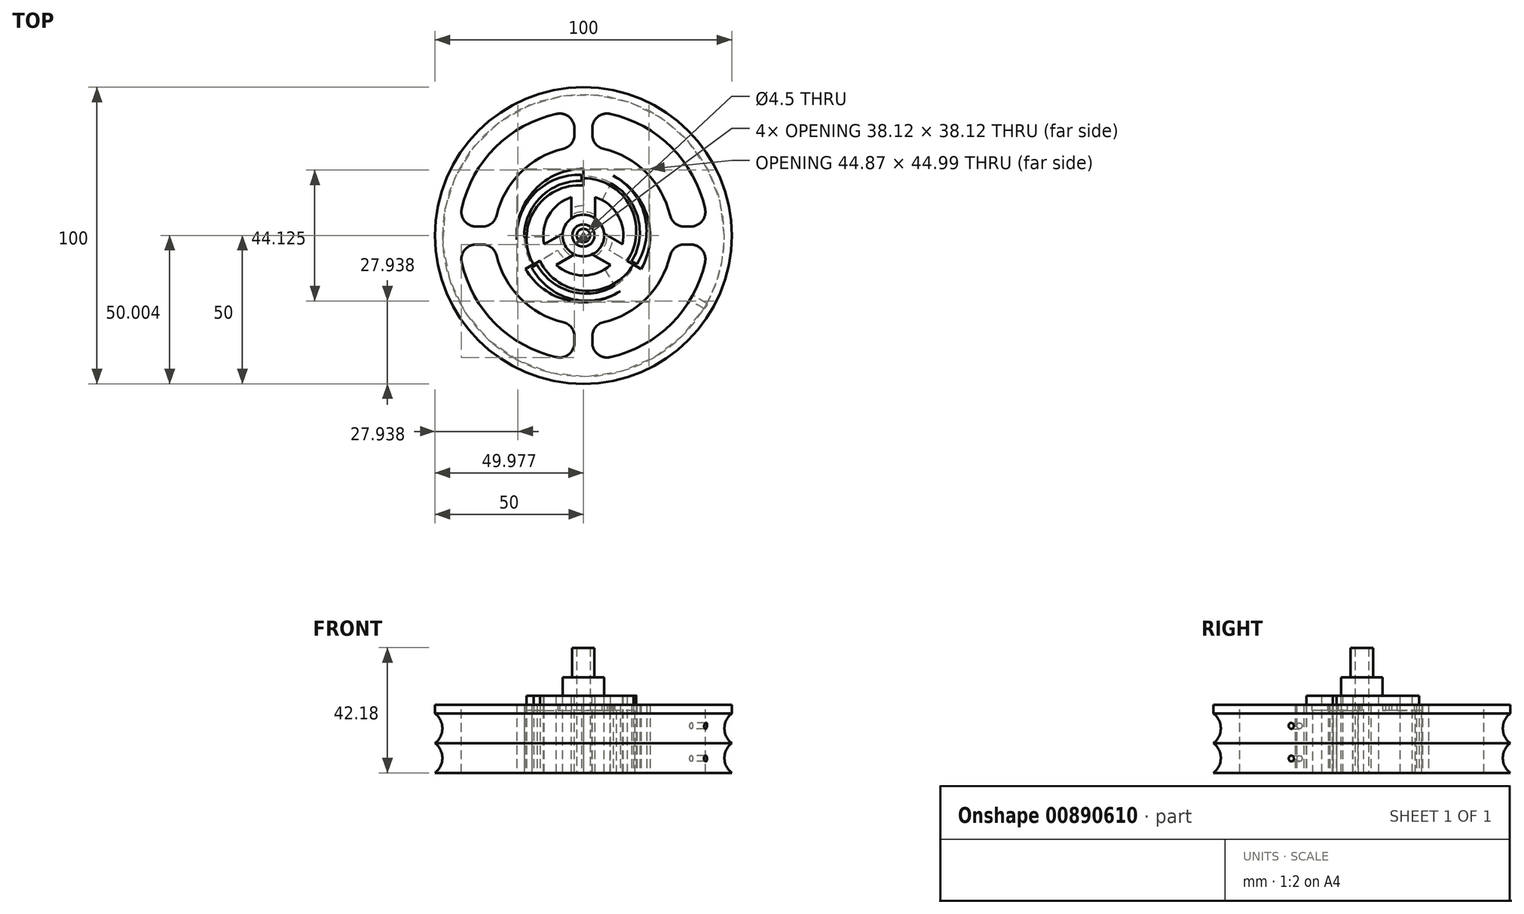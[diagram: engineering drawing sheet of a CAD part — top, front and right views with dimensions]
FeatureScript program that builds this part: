
annotation { "Feature Type Name" : "Feature", "Feature Type Description" : "" }
export const myFeature = defineFeature(function(context is Context, id is Id, definition is map)
    precondition{}
    {
        {
            var Q0;
            Q0=qCreatedBy(makeId("Top.planeOp"),FACE);
            var sketch = newSketch(context, id + "F0", { "sketchPlane" : qUnion([Q0])});
            skCircle(sketch, "E0", {"center": v(0, 0) * mm, "radius": 50 * mm});
            skLineSegment(sketch, "E1", {"start": v(0.67, 20.46) * mm, "end": v(0.67, 18.46) * mm});
            skArc(sketch, "E2", {"start": v(22.46, -1.4) * mm, "mid": v(16.36, 14.31) * mm, "end": v(0.67, 20.46) * mm});
            skArc(sketch, "E3", {"start": v(19.96, -1.24) * mm, "mid": v(14.55, 12.75) * mm, "end": v(0.67, 18.46) * mm});
            skArc(sketch, "E4", {"start": v(22.46, -1.4) * mm, "mid": v(16.4, 15.4) * mm, "end": v(0, 22.5) * mm});
            skArc(sketch, "E5", {"start": v(17.32, -10) * mm, "mid": v(19.15, -5.77) * mm, "end": v(19.96, -1.24) * mm});
            skLineSegment(sketch, "E6", {"start": v(0, 22.5) * mm, "end": v(0, 20) * mm});
            skArc(sketch, "E7.1.0", {"start": v(-10.02, 20.15) * mm, "mid": v(-21.54, 6.5) * mm, "end": v(-19.49, -11.25) * mm});
            skArc(sketch, "E7.1.1", {"start": v(0, 20) * mm, "mid": v(-4.58, 19.47) * mm, "end": v(-8.9, 17.9) * mm});
            skArc(sketch, "E7.1.2", {"start": v(-10.02, 20.15) * mm, "mid": v(-20.57, 7.01) * mm, "end": v(-18.05, -9.65) * mm});
            skArc(sketch, "E7.1.3", {"start": v(-8.9, 17.9) * mm, "mid": v(-18.32, 6.22) * mm, "end": v(-16.32, -8.65) * mm});
            skLineSegment(sketch, "E7.1.4", {"start": v(-18.05, -9.65) * mm, "end": v(-16.32, -8.65) * mm});
            skLineSegment(sketch, "E7.1.5", {"start": v(-19.49, -11.25) * mm, "end": v(-17.32, -10) * mm});
            skArc(sketch, "E7.2.0", {"start": v(-12.44, -18.75) * mm, "mid": v(5.15, -21.9) * mm, "end": v(19.49, -11.25) * mm});
            skArc(sketch, "E7.2.1", {"start": v(-17.32, -10) * mm, "mid": v(-14.57, -13.7) * mm, "end": v(-11.05, -16.67) * mm});
            skArc(sketch, "E7.2.2", {"start": v(-12.44, -18.75) * mm, "mid": v(4.21, -21.32) * mm, "end": v(17.38, -10.81) * mm});
            skArc(sketch, "E7.2.3", {"start": v(-11.05, -16.67) * mm, "mid": v(3.77, -18.98) * mm, "end": v(15.65, -9.81) * mm});
            skLineSegment(sketch, "E7.2.4", {"start": v(17.38, -10.81) * mm, "end": v(15.65, -9.81) * mm});
            skLineSegment(sketch, "E7.2.5", {"start": v(19.49, -11.25) * mm, "end": v(17.32, -10) * mm});
            skLineSegment(sketch, "E8", {"start": v(0, 19.35) * mm, "end": v(0, 16.88) * mm});
            skLineSegment(sketch, "E9", {"start": v(-17.32, -10) * mm, "end": v(0, 0) * mm, "construction": true});
            skArc(sketch, "E10", {"start": v(0, 19.35) * mm, "mid": v(-15.76, 9.87) * mm, "end": v(-14.71, -8.5) * mm});
            skArc(sketch, "E11.1.0", {"start": v(-16.85, -9.73) * mm, "mid": v(-0.76, -18.64) * mm, "end": v(14.62, -8.55) * mm});
            skLineSegment(sketch, "E11.1.1", {"start": v(-16.85, -9.73) * mm, "end": v(-14.71, -8.5) * mm});
            skArc(sketch, "E11.2.0", {"start": v(16.76, -9.78) * mm, "mid": v(16.43, 8.6) * mm, "end": v(0, 16.88) * mm});
            skLineSegment(sketch, "E11.2.1", {"start": v(16.76, -9.78) * mm, "end": v(14.62, -8.55) * mm});
            skPoint(sketch, "E11.center", {"position": v(-0.03, -0.05) * mm});
            skLineSegment(sketch, "E12", {"start": v(-16.85, -9.73) * mm, "end": v(-17.19, -9.15) * mm, "construction": true});
            skLineSegment(sketch, "E13", {"start": v(0, 0) * mm, "end": v(22.46, -1.4) * mm, "construction": true});
            skLineSegment(sketch, "E14.1.0", {"start": v(0, 0) * mm, "end": v(-10.02, 20.15) * mm, "construction": true});
            skLineSegment(sketch, "E14.2.0", {"start": v(0, 0) * mm, "end": v(-12.44, -18.75) * mm, "construction": true});
            skLineSegment(sketch, "E15.1.0", {"start": v(17.32, -10) * mm, "end": v(0, 0) * mm, "construction": true});
            skLineSegment(sketch, "E15.2.0", {"start": v(0, 20) * mm, "end": v(0, 0) * mm, "construction": true});
            skSolve(sketch);
        }
        {
            var Q0;
            Q0=makeQuery(id+"F0.imprint","IMPRINT",FACE,{"disambiguationData":[TD([[makeQuery(id+"F0.imprint","IMPRINT",EDGE,{"derivedFrom":sQuery(id+"F0.wireOp",EDGE,"E0")}),1.0]])]});
            extrude(context, id + "F1", {"entities" : qUnion([Q0]), "depth" : 21 * mm, "offsetDistance" : 25 * mm});
        }
        {
            var Q0;
            {var subQ3=sQuery(id+"F0.wireOp",EDGE,"E10");var subQ7=sQuery(id+"F0.wireOp",EDGE,"E8");var subQ8=makeQuery(id+"F0.imprint","INTERSECT",VERTEX,{"derivedFrom":[subQ7,subQ3]});Q0=makeQuery(id+"F0.imprint","IMPRINT",FACE,{"disambiguationData":[TD([[makeQuery(id+"F0.imprint","IMPRINT",EDGE,{"disambiguationData":[TD([[subQ8,-1.0]])],"derivedFrom":subQ7}),-1.0]])]});}
            extrude(context, id + "F2", {"entities" : qUnion([Q0]), "depth" : 26 * mm, "offsetDistance" : 25 * mm});
        }
        {
            var Q0;
            Q0=qCreatedBy(makeId("Right.planeOp"),FACE);
            var sketch = newSketch(context, id + "F3", { "sketchPlane" : qUnion([Q0])});
            skLineSegment(sketch, "E16", {"start": v(0, 0) * mm, "end": v(50, 0) * mm});
            skLineSegment(sketch, "E17", {"start": v(50, 0) * mm, "end": v(50, 20) * mm});
            skLineSegment(sketch, "E18", {"start": v(50, 20) * mm, "end": v(0, 20) * mm});
            skLineSegment(sketch, "E19", {"start": v(0, 20) * mm, "end": v(0, 0) * mm});
            skArc(sketch, "E20", {"start": v(50, 20) * mm, "mid": v(47.53, 15) * mm, "end": v(50, 10) * mm});
            skArc(sketch, "E21", {"start": v(50, 10) * mm, "mid": v(47.53, 5) * mm, "end": v(50, 0) * mm});
            skSolve(sketch);
        }
        {
            var Q0;
            {var subQ0=sQuery(id+"F3.wireOp",EDGE,"E20");Q0=makeQuery(id+"F3.imprint","IMPRINT",FACE,{"disambiguationData":[TD([[makeQuery(id+"F3.imprint","IMPRINT",EDGE,{"derivedFrom":subQ0}),1.0]])]});}
            var Q1;
            {var subQ0=sQuery(id+"F3.wireOp",EDGE,"E21");Q1=makeQuery(id+"F3.imprint","IMPRINT",FACE,{"disambiguationData":[TD([[makeQuery(id+"F3.imprint","IMPRINT",EDGE,{"derivedFrom":subQ0}),1.0]])]});}
            var Q2;
            Q2=sQuery(id+"F3.wireOp",EDGE,"E19");
            revolve(context, id + "F4", {"operationType" : NewBodyOperationType.REMOVE, "surfaceOperationType" : NewSurfaceOperationType.NEW, "entities" : qUnion([Q0, Q1]), "axis" : qUnion([Q2]), "revolveType" : RevolveType.FULL, "oppositeDirection" : true});
        }
        {
            var Q0;
            Q0=makeQuery(id+"F2.opExtrude","CAP_FACE",FACE,{"disambiguationData":[OSD([sQuery(id+"F0.wireOp",EDGE,"E8"),sQuery(id+"F0.wireOp",EDGE,"E10"),sQuery(id+"F0.wireOp",EDGE,"E11.1.0"),sQuery(id+"F0.wireOp",EDGE,"E11.1.1"),sQuery(id+"F0.wireOp",EDGE,"E11.2.0"),sQuery(id+"F0.wireOp",EDGE,"E11.2.1")])],"isStart":true});
            var sketch = newSketch(context, id + "F5", { "sketchPlane" : qUnion([Q0])});
            skCircle(sketch, "E22", {"center": v(0, 0) * mm, "radius": 2.25 * mm});
            skSolve(sketch);
        }
        {
            var Q0;
            Q0=makeQuery(id+"F5.imprint","IMPRINT",FACE,{"disambiguationData":[TD([[makeQuery(id+"F5.imprint","IMPRINT",EDGE,{"derivedFrom":sQuery(id+"F5.wireOp",EDGE,"E22")}),1.0]])]});
            extrude(context, id + "F6", {"entities" : qUnion([Q0]), "operationType" : NewBodyOperationType.REMOVE, "oppositeDirection" : true, "depth" : 100 * mm, "offsetDistance" : 25 * mm});
        }
        {
            var Q0;
            Q0=qCreatedBy(makeId("Right.planeOp"),FACE);
            cPlane(context, id + "F7", {"entities" : qUnion([Q0]), "cplaneType" : CPlaneType.OFFSET, "offset" : 50 * mm, "width" : 150 * mm, "height" : 150 * mm});
        }
        {
            var Q0;
            Q0=makeQuery(id+"F2.opExtrude","SWEPT_BODY",BODY,{"disambiguationData":[OSD([sQuery(id+"F0.wireOp",EDGE,"E8"),sQuery(id+"F0.wireOp",EDGE,"E10"),sQuery(id+"F0.wireOp",EDGE,"E11.1.0"),sQuery(id+"F0.wireOp",EDGE,"E11.1.1"),sQuery(id+"F0.wireOp",EDGE,"E11.2.0"),sQuery(id+"F0.wireOp",EDGE,"E11.2.1")])]});
            var Q1;
            Q1=makeQuery(id+"F1.opExtrude","SWEPT_BODY",BODY,{"disambiguationData":[OSD([sQuery(id+"F0.wireOp",EDGE,"E0"),sQuery(id+"F0.wireOp",EDGE,"E1"),sQuery(id+"F0.wireOp",EDGE,"E2"),sQuery(id+"F0.wireOp",EDGE,"E3"),sQuery(id+"F0.wireOp",EDGE,"E4"),sQuery(id+"F0.wireOp",EDGE,"E5"),sQuery(id+"F0.wireOp",EDGE,"E6"),sQuery(id+"F0.wireOp",EDGE,"E7.1.0"),sQuery(id+"F0.wireOp",EDGE,"E7.1.1"),sQuery(id+"F0.wireOp",EDGE,"E7.1.2"),sQuery(id+"F0.wireOp",EDGE,"E7.1.3"),sQuery(id+"F0.wireOp",EDGE,"E7.1.4"),sQuery(id+"F0.wireOp",EDGE,"E7.1.5"),sQuery(id+"F0.wireOp",EDGE,"E7.2.0"),sQuery(id+"F0.wireOp",EDGE,"E7.2.1"),sQuery(id+"F0.wireOp",EDGE,"E7.2.2"),sQuery(id+"F0.wireOp",EDGE,"E7.2.3"),sQuery(id+"F0.wireOp",EDGE,"E7.2.4"),sQuery(id+"F0.wireOp",EDGE,"E7.2.5")])]});
            var Q2;
            Q2=qCreatedBy(id+"F7.planeOp",FACE);
            mirror(context, id + "F8", {"entities" : qUnion([Q0, Q1]), "mirrorPlane" : qUnion([Q2])});
        }
        {
            var Q0;
            Q0=makeQuery(id+"F8.opPattern","COPY",BODY,{"derivedFrom":makeQuery(id+"F2.opExtrude","SWEPT_BODY",BODY,{"disambiguationData":[OSD([sQuery(id+"F0.wireOp",EDGE,"E8"),sQuery(id+"F0.wireOp",EDGE,"E10"),sQuery(id+"F0.wireOp",EDGE,"E11.1.0"),sQuery(id+"F0.wireOp",EDGE,"E11.1.1"),sQuery(id+"F0.wireOp",EDGE,"E11.2.0"),sQuery(id+"F0.wireOp",EDGE,"E11.2.1")])]}),"instanceName":"1"});
            var Q1;
            Q1=makeQuery(id+"F8.opPattern","COPY",BODY,{"derivedFrom":makeQuery(id+"F1.opExtrude","SWEPT_BODY",BODY,{"disambiguationData":[OSD([sQuery(id+"F0.wireOp",EDGE,"E0"),sQuery(id+"F0.wireOp",EDGE,"E1"),sQuery(id+"F0.wireOp",EDGE,"E2"),sQuery(id+"F0.wireOp",EDGE,"E3"),sQuery(id+"F0.wireOp",EDGE,"E4"),sQuery(id+"F0.wireOp",EDGE,"E5"),sQuery(id+"F0.wireOp",EDGE,"E6"),sQuery(id+"F0.wireOp",EDGE,"E7.1.0"),sQuery(id+"F0.wireOp",EDGE,"E7.1.1"),sQuery(id+"F0.wireOp",EDGE,"E7.1.2"),sQuery(id+"F0.wireOp",EDGE,"E7.1.3"),sQuery(id+"F0.wireOp",EDGE,"E7.1.4"),sQuery(id+"F0.wireOp",EDGE,"E7.1.5"),sQuery(id+"F0.wireOp",EDGE,"E7.2.0"),sQuery(id+"F0.wireOp",EDGE,"E7.2.1"),sQuery(id+"F0.wireOp",EDGE,"E7.2.2"),sQuery(id+"F0.wireOp",EDGE,"E7.2.3"),sQuery(id+"F0.wireOp",EDGE,"E7.2.4"),sQuery(id+"F0.wireOp",EDGE,"E7.2.5")])]}),"instanceName":"1"});
            var Q2;
            Q2=qCreatedBy(id+"F7.planeOp",FACE);
            mirror(context, id + "F9", {"operationType" : NewBodyOperationType.REMOVE, "entities" : qUnion([Q0, Q1]), "mirrorPlane" : qUnion([Q2])});
        }
        {
            var Q0;
            Q0=makeQuery(id+"F8.opPattern","COPY",BODY,{"derivedFrom":makeQuery(id+"F2.opExtrude","SWEPT_BODY",BODY,{"disambiguationData":[OSD([sQuery(id+"F0.wireOp",EDGE,"E8"),sQuery(id+"F0.wireOp",EDGE,"E10"),sQuery(id+"F0.wireOp",EDGE,"E11.1.0"),sQuery(id+"F0.wireOp",EDGE,"E11.1.1"),sQuery(id+"F0.wireOp",EDGE,"E11.2.0"),sQuery(id+"F0.wireOp",EDGE,"E11.2.1")])]}),"instanceName":"1"});
            var Q1;
            Q1=makeQuery(id+"F8.opPattern","COPY",BODY,{"derivedFrom":makeQuery(id+"F1.opExtrude","SWEPT_BODY",BODY,{"disambiguationData":[OSD([sQuery(id+"F0.wireOp",EDGE,"E0"),sQuery(id+"F0.wireOp",EDGE,"E1"),sQuery(id+"F0.wireOp",EDGE,"E2"),sQuery(id+"F0.wireOp",EDGE,"E3"),sQuery(id+"F0.wireOp",EDGE,"E4"),sQuery(id+"F0.wireOp",EDGE,"E5"),sQuery(id+"F0.wireOp",EDGE,"E6"),sQuery(id+"F0.wireOp",EDGE,"E7.1.0"),sQuery(id+"F0.wireOp",EDGE,"E7.1.1"),sQuery(id+"F0.wireOp",EDGE,"E7.1.2"),sQuery(id+"F0.wireOp",EDGE,"E7.1.3"),sQuery(id+"F0.wireOp",EDGE,"E7.1.4"),sQuery(id+"F0.wireOp",EDGE,"E7.1.5"),sQuery(id+"F0.wireOp",EDGE,"E7.2.0"),sQuery(id+"F0.wireOp",EDGE,"E7.2.1"),sQuery(id+"F0.wireOp",EDGE,"E7.2.2"),sQuery(id+"F0.wireOp",EDGE,"E7.2.3"),sQuery(id+"F0.wireOp",EDGE,"E7.2.4"),sQuery(id+"F0.wireOp",EDGE,"E7.2.5")])]}),"instanceName":"1"});
            transform(context, id + "F10", {"entities" : qUnion([Q0, Q1]), "transformType" : TransformType.TRANSLATION_3D, "dx" : -100 * mm, "dy" : 0 * mm, "dz" : 0 * mm, "makeCopy" : false});
        }
        {
            var Q0;
            Q0=makeQuery(id+"F8.opPattern","COPY",FACE,{"derivedFrom":makeQuery(id+"F1.opExtrude","CAP_FACE",FACE,{"disambiguationData":[OSD([sQuery(id+"F0.wireOp",EDGE,"E0"),sQuery(id+"F0.wireOp",EDGE,"E1"),sQuery(id+"F0.wireOp",EDGE,"E2"),sQuery(id+"F0.wireOp",EDGE,"E3"),sQuery(id+"F0.wireOp",EDGE,"E4"),sQuery(id+"F0.wireOp",EDGE,"E5"),sQuery(id+"F0.wireOp",EDGE,"E6"),sQuery(id+"F0.wireOp",EDGE,"E7.1.0"),sQuery(id+"F0.wireOp",EDGE,"E7.1.1"),sQuery(id+"F0.wireOp",EDGE,"E7.1.2"),sQuery(id+"F0.wireOp",EDGE,"E7.1.3"),sQuery(id+"F0.wireOp",EDGE,"E7.1.4"),sQuery(id+"F0.wireOp",EDGE,"E7.1.5"),sQuery(id+"F0.wireOp",EDGE,"E7.2.0"),sQuery(id+"F0.wireOp",EDGE,"E7.2.1"),sQuery(id+"F0.wireOp",EDGE,"E7.2.2"),sQuery(id+"F0.wireOp",EDGE,"E7.2.3"),sQuery(id+"F0.wireOp",EDGE,"E7.2.4"),sQuery(id+"F0.wireOp",EDGE,"E7.2.5")])],"isStart":false}),"instanceName":"1"});
            var sketch = newSketch(context, id + "F11", { "sketchPlane" : qUnion([Q0])});
            skCircle(sketch, "E23", {"center": v(0, 0) * mm, "radius": 8 * mm});
            skCircle(sketch, "E24", {"center": v(0, 0) * mm, "radius": 10 * mm});
            skLineSegment(sketch, "E25", {"start": v(0, 20) * mm, "end": v(0, 10) * mm});
            skLineSegment(sketch, "E26", {"start": v(0, 10) * mm, "end": v(0, 0) * mm, "construction": true});
            skLineSegment(sketch, "E27", {"start": v(4.7, 8.83) * mm, "end": v(0, 0) * mm, "construction": true});
            skLineSegment(sketch, "E28", {"start": v(4.7, 8.83) * mm, "end": v(9.38, 17.65) * mm});
            skLineSegment(sketch, "E29.1.0", {"start": v(-17.32, -10) * mm, "end": v(-8.66, -5) * mm});
            skLineSegment(sketch, "E29.1.1", {"start": v(-10, -0.35) * mm, "end": v(-19.97, -0.7) * mm});
            skLineSegment(sketch, "E29.1.2", {"start": v(-10, -0.35) * mm, "end": v(0, 0) * mm, "construction": true});
            skLineSegment(sketch, "E29.1.3", {"start": v(-8.66, -5) * mm, "end": v(0, 0) * mm, "construction": true});
            skLineSegment(sketch, "E29.2.0", {"start": v(17.32, -10) * mm, "end": v(8.66, -5) * mm});
            skLineSegment(sketch, "E29.2.1", {"start": v(5.3, -8.48) * mm, "end": v(10.6, -16.95) * mm});
            skLineSegment(sketch, "E29.2.2", {"start": v(5.3, -8.48) * mm, "end": v(0, 0) * mm, "construction": true});
            skLineSegment(sketch, "E29.2.3", {"start": v(8.66, -5) * mm, "end": v(0, 0) * mm, "construction": true});
            skSolve(sketch);
        }
        {
            var Q0;
            Q0=makeQuery(id+"F11.imprint","IMPRINT",FACE,{"disambiguationData":[TD([[makeQuery(id+"F11.imprint","IMPRINT",EDGE,{"derivedFrom":makeQuery(id+"F8.opPattern","COPY",EDGE,{"derivedFrom":makeQuery(id+"F1.opExtrude","CAP_EDGE",EDGE,{"disambiguationData":[OSD([sQuery(id+"F0.wireOp",EDGE,"E0")])],"isStart":false}),"instanceName":"1"})}),-1.0]])]});
            var Q1;
            Q1=makeQuery(id+"F11.imprint","IMPRINT",FACE,{"disambiguationData":[TD([[makeQuery(id+"F11.imprint","IMPRINT",EDGE,{"derivedFrom":sQuery(id+"F11.wireOp",EDGE,"E23")}),-1.0]])]});
            var Q2;
            {var subQ0=sQuery(id+"F11.wireOp",EDGE,"E25");Q2=makeQuery(id+"F11.imprint","IMPRINT",FACE,{"disambiguationData":[TD([[makeQuery(id+"F11.imprint","IMPRINT",EDGE,{"derivedFrom":subQ0}),1.0]])]});}
            var Q3;
            {var subQ0=sQuery(id+"F11.wireOp",EDGE,"3a16bb13-5f1d-4999-a017-b99e6dc903f3.2.2");Q3=makeQuery(id+"F11.imprint","IMPRINT",FACE,{"disambiguationData":[TD([[makeQuery(id+"F11.imprint","IMPRINT",EDGE,{"derivedFrom":subQ0}),1.0]])]});}
            var Q4;
            {var subQ0=sQuery(id+"F11.wireOp",EDGE,"3a16bb13-5f1d-4999-a017-b99e6dc903f3.1.2");Q4=makeQuery(id+"F11.imprint","IMPRINT",FACE,{"disambiguationData":[TD([[makeQuery(id+"F11.imprint","IMPRINT",EDGE,{"derivedFrom":subQ0}),1.0]])]});}
            var Q5;
            {var subQ0=sQuery(id+"F11.wireOp",EDGE,"E29.1.0");Q5=makeQuery(id+"F11.imprint","IMPRINT",FACE,{"disambiguationData":[TD([[makeQuery(id+"F11.imprint","IMPRINT",EDGE,{"derivedFrom":subQ0}),1.0]])]});}
            var Q6;
            {var subQ1=sQuery(id+"F11.wireOp",EDGE,"E29.2.0");Q6=makeQuery(id+"F11.imprint","IMPRINT",FACE,{"disambiguationData":[TD([[makeQuery(id+"F11.imprint","IMPRINT",EDGE,{"derivedFrom":subQ1}),1.0]])]});}
            extrude(context, id + "F12", {"entities" : qUnion([Q0, Q1, Q2, Q3, Q4, Q5, Q6]), "depth" : 2 * mm, "offsetDistance" : 25 * mm});
        }
        {
            var Q0;
            Q0=makeQuery(id+"F8.opPattern","COPY",BODY,{"derivedFrom":makeQuery(id+"F1.opExtrude","SWEPT_BODY",BODY,{"disambiguationData":[OSD([sQuery(id+"F0.wireOp",EDGE,"E0"),sQuery(id+"F0.wireOp",EDGE,"E1"),sQuery(id+"F0.wireOp",EDGE,"E2"),sQuery(id+"F0.wireOp",EDGE,"E3"),sQuery(id+"F0.wireOp",EDGE,"E4"),sQuery(id+"F0.wireOp",EDGE,"E5"),sQuery(id+"F0.wireOp",EDGE,"E6"),sQuery(id+"F0.wireOp",EDGE,"E7.1.0"),sQuery(id+"F0.wireOp",EDGE,"E7.1.1"),sQuery(id+"F0.wireOp",EDGE,"E7.1.2"),sQuery(id+"F0.wireOp",EDGE,"E7.1.3"),sQuery(id+"F0.wireOp",EDGE,"E7.1.4"),sQuery(id+"F0.wireOp",EDGE,"E7.1.5"),sQuery(id+"F0.wireOp",EDGE,"E7.2.0"),sQuery(id+"F0.wireOp",EDGE,"E7.2.1"),sQuery(id+"F0.wireOp",EDGE,"E7.2.2"),sQuery(id+"F0.wireOp",EDGE,"E7.2.3"),sQuery(id+"F0.wireOp",EDGE,"E7.2.4"),sQuery(id+"F0.wireOp",EDGE,"E7.2.5")])]}),"instanceName":"1"});
            var Q1;
            Q1=makeQuery(id+"F12.opExtrude","SWEPT_BODY",BODY,{"disambiguationData":[OSD([sQuery(id+"F0.wireOp",EDGE,"E0"),sQuery(id+"F0.wireOp",EDGE,"E1"),sQuery(id+"F0.wireOp",EDGE,"E2"),sQuery(id+"F0.wireOp",EDGE,"E3"),sQuery(id+"F0.wireOp",EDGE,"E4"),sQuery(id+"F0.wireOp",EDGE,"E6"),sQuery(id+"F0.wireOp",EDGE,"E7.1.0"),sQuery(id+"F0.wireOp",EDGE,"E7.1.2"),sQuery(id+"F0.wireOp",EDGE,"E7.1.3"),sQuery(id+"F0.wireOp",EDGE,"E7.1.4"),sQuery(id+"F0.wireOp",EDGE,"E7.1.5"),sQuery(id+"F0.wireOp",EDGE,"E7.2.0"),sQuery(id+"F0.wireOp",EDGE,"E7.2.2"),sQuery(id+"F0.wireOp",EDGE,"E7.2.3"),sQuery(id+"F0.wireOp",EDGE,"E7.2.4"),sQuery(id+"F0.wireOp",EDGE,"E7.2.5"),sQuery(id+"F11.wireOp",EDGE,"E23"),sQuery(id+"F11.wireOp",EDGE,"E24"),sQuery(id+"F11.wireOp",EDGE,"E25"),sQuery(id+"F11.wireOp",EDGE,"78l2gyW1-TRG6-uo8H-a0o9-FiCq7i56H5jk"),sQuery(id+"F11.wireOp",EDGE,"3a16bb13-5f1d-4999-a017-b99e6dc903f3.1.2"),sQuery(id+"F11.wireOp",EDGE,"3a16bb13-5f1d-4999-a017-b99e6dc903f3.1.3"),sQuery(id+"F11.wireOp",EDGE,"3a16bb13-5f1d-4999-a017-b99e6dc903f3.2.2"),sQuery(id+"F11.wireOp",EDGE,"3a16bb13-5f1d-4999-a017-b99e6dc903f3.2.3")])]});
            booleanBodies(context, id + "F13", {"operationType" : BooleanOperationType.UNION, "tools" : qUnion([Q0, Q1])});
        }
        {
            var Q0;
            Q0=makeQuery(id+"F8.opPattern","COPY",FACE,{"derivedFrom":makeQuery(id+"F2.opExtrude","CAP_FACE",FACE,{"disambiguationData":[OSD([sQuery(id+"F0.wireOp",EDGE,"E8"),sQuery(id+"F0.wireOp",EDGE,"E10"),sQuery(id+"F0.wireOp",EDGE,"E11.1.0"),sQuery(id+"F0.wireOp",EDGE,"E11.1.1"),sQuery(id+"F0.wireOp",EDGE,"E11.2.0"),sQuery(id+"F0.wireOp",EDGE,"E11.2.1")])],"isStart":false}),"instanceName":"1"});
            var sketch = newSketch(context, id + "F14", { "sketchPlane" : qUnion([Q0])});
            skCircle(sketch, "E30", {"center": v(0, 0) * mm, "radius": 13.5 * mm});
            skCircle(sketch, "E31", {"center": v(0, 0) * mm, "radius": 7 * mm});
            skLineSegment(sketch, "E32", {"start": v(-4, 12.9) * mm, "end": v(-4, 5.74) * mm});
            skLineSegment(sketch, "E33", {"start": v(4, 12.9) * mm, "end": v(4, 5.74) * mm});
            skLineSegment(sketch, "E34.1.0", {"start": v(-9.17, -9.91) * mm, "end": v(-2.97, -6.34) * mm});
            skLineSegment(sketch, "E34.1.1", {"start": v(-13.17, -2.98) * mm, "end": v(-6.97, 0.6) * mm});
            skLineSegment(sketch, "E34.2.0", {"start": v(13.17, -2.98) * mm, "end": v(6.97, 0.6) * mm});
            skLineSegment(sketch, "E34.2.1", {"start": v(9.17, -9.91) * mm, "end": v(2.97, -6.34) * mm});
            skCircle(sketch, "E35", {"center": v(0, 0) * mm, "radius": 3.75 * mm});
            skSolve(sketch);
        }
        {
            var Q0;
            {var subQ0=sQuery(id+"F14.wireOp",EDGE,"E32");Q0=makeQuery(id+"F14.imprint","IMPRINT",FACE,{"disambiguationData":[TD([[makeQuery(id+"F14.imprint","IMPRINT",EDGE,{"derivedFrom":subQ0}),-1.0]])]});}
            var Q1;
            {var subQ0=sQuery(id+"F14.wireOp",EDGE,"E34.1.0");Q1=makeQuery(id+"F14.imprint","IMPRINT",FACE,{"disambiguationData":[TD([[makeQuery(id+"F14.imprint","IMPRINT",EDGE,{"derivedFrom":subQ0}),-1.0]])]});}
            var Q2;
            {var subQ0=sQuery(id+"F14.wireOp",EDGE,"E33");Q2=makeQuery(id+"F14.imprint","IMPRINT",FACE,{"disambiguationData":[TD([[makeQuery(id+"F14.imprint","IMPRINT",EDGE,{"derivedFrom":subQ0}),1.0]])]});}
            var Q3;
            Q3=makeQuery(id+"F8.opPattern","COPY",FACE,{"derivedFrom":makeQuery(id+"F2.opExtrude","CAP_FACE",FACE,{"disambiguationData":[OSD([sQuery(id+"F0.wireOp",EDGE,"E8"),sQuery(id+"F0.wireOp",EDGE,"E10"),sQuery(id+"F0.wireOp",EDGE,"E11.1.0"),sQuery(id+"F0.wireOp",EDGE,"E11.1.1"),sQuery(id+"F0.wireOp",EDGE,"E11.2.0"),sQuery(id+"F0.wireOp",EDGE,"E11.2.1")])],"isStart":true}),"instanceName":"1"});
            extrude(context, id + "F15", {"entities" : qUnion([Q0, Q1, Q2]), "operationType" : NewBodyOperationType.REMOVE, "endBound" : BoundingType.UP_TO_SURFACE, "oppositeDirection" : true, "depth" : 25 * mm, "endBoundEntityFace" : qUnion([Q3]), "offsetDistance" : 25 * mm});
        }
        {
            var Q0;
            {var subQ0=sQuery(id+"F14.wireOp",EDGE,"E31");var subQ4=makeQuery(id+"F14.imprint","INTERSECT",VERTEX,{"derivedFrom":[subQ0,sQuery(id+"F14.wireOp",EDGE,"E33")]});Q0=makeQuery(id+"F14.imprint","IMPRINT",FACE,{"disambiguationData":[TD([[makeQuery(id+"F14.imprint","IMPRINT",EDGE,{"disambiguationData":[TD([[subQ4,1.0]])],"derivedFrom":subQ0}),1.0]])]});}
            extrude(context, id + "F16", {"entities" : qUnion([Q0]), "operationType" : NewBodyOperationType.ADD, "depth" : 6.16 * mm, "offsetDistance" : 25 * mm});
        }
        {
            var Q0;
            Q0=makeQuery(id+"F14.imprint","IMPRINT",FACE,{"disambiguationData":[TD([[makeQuery(id+"F14.imprint","IMPRINT",EDGE,{"derivedFrom":sQuery(id+"F14.wireOp",EDGE,"E35")}),1.0]])]});
            extrude(context, id + "F17", {"entities" : qUnion([Q0]), "operationType" : NewBodyOperationType.ADD, "depth" : 16.18 * mm, "offsetDistance" : 25 * mm});
        }
        {
            var Q0;
            Q0=makeQuery(id+"F12.opExtrude","CAP_FACE",FACE,{"disambiguationData":[OSD([sQuery(id+"F0.wireOp",EDGE,"E0"),sQuery(id+"F0.wireOp",EDGE,"E1"),sQuery(id+"F0.wireOp",EDGE,"E2"),sQuery(id+"F0.wireOp",EDGE,"E3"),sQuery(id+"F0.wireOp",EDGE,"E4"),sQuery(id+"F0.wireOp",EDGE,"E6"),sQuery(id+"F0.wireOp",EDGE,"E7.1.0"),sQuery(id+"F0.wireOp",EDGE,"E7.1.2"),sQuery(id+"F0.wireOp",EDGE,"E7.1.3"),sQuery(id+"F0.wireOp",EDGE,"E7.1.4"),sQuery(id+"F0.wireOp",EDGE,"E7.1.5"),sQuery(id+"F0.wireOp",EDGE,"E7.2.0"),sQuery(id+"F0.wireOp",EDGE,"E7.2.2"),sQuery(id+"F0.wireOp",EDGE,"E7.2.3"),sQuery(id+"F0.wireOp",EDGE,"E7.2.4"),sQuery(id+"F0.wireOp",EDGE,"E7.2.5"),sQuery(id+"F11.wireOp",EDGE,"E23"),sQuery(id+"F11.wireOp",EDGE,"E24"),sQuery(id+"F11.wireOp",EDGE,"E25"),sQuery(id+"F11.wireOp",EDGE,"E28"),sQuery(id+"F11.wireOp",EDGE,"E29.1.0"),sQuery(id+"F11.wireOp",EDGE,"E29.1.1"),sQuery(id+"F11.wireOp",EDGE,"E29.2.0"),sQuery(id+"F11.wireOp",EDGE,"E29.2.1")])],"isStart":false});
            var sketch = newSketch(context, id + "F18", { "sketchPlane" : qUnion([Q0])});
            skCircle(sketch, "E36", {"center": v(0, 0) * mm, "radius": 42 * mm});
            skCircle(sketch, "E37", {"center": v(0, 0) * mm, "radius": 30 * mm});
            skLineSegment(sketch, "E38", {"start": v(0, 0) * mm, "end": v(0, 50) * mm, "construction": true});
            skLineSegment(sketch, "E39", {"start": v(0, 0) * mm, "end": v(42, 0) * mm, "construction": true});
            skLineSegment(sketch, "E40", {"start": v(0, 0) * mm, "end": v(0, -42) * mm, "construction": true});
            skLineSegment(sketch, "E41", {"start": v(0, 0) * mm, "end": v(-42, 0) * mm, "construction": true});
            skLineSegment(sketch, "E42", {"start": v(-3, 41.9) * mm, "end": v(-3, 29.85) * mm});
            skLineSegment(sketch, "E43", {"start": v(3, 41.9) * mm, "end": v(3, 29.85) * mm});
            skLineSegment(sketch, "E44.1.0", {"start": v(-41.9, 3) * mm, "end": v(-29.85, 3) * mm});
            skLineSegment(sketch, "E44.1.1", {"start": v(-41.9, -3) * mm, "end": v(-29.85, -3) * mm});
            skLineSegment(sketch, "E44.2.0", {"start": v(-3, -41.9) * mm, "end": v(-3, -29.85) * mm});
            skLineSegment(sketch, "E44.2.1", {"start": v(3, -41.9) * mm, "end": v(3, -29.85) * mm});
            skLineSegment(sketch, "E44.3.0", {"start": v(41.9, -3) * mm, "end": v(29.85, -3) * mm});
            skLineSegment(sketch, "E44.3.1", {"start": v(41.9, 3) * mm, "end": v(29.85, 3) * mm});
            skSolve(sketch);
        }
        {
            var Q0;
            {var subQ0=sQuery(id+"F18.wireOp",EDGE,"E42");Q0=makeQuery(id+"F18.imprint","IMPRINT",FACE,{"disambiguationData":[TD([[makeQuery(id+"F18.imprint","IMPRINT",EDGE,{"derivedFrom":subQ0}),-1.0]])]});}
            var Q1;
            {var subQ0=sQuery(id+"F18.wireOp",EDGE,"E44.1.1");Q1=makeQuery(id+"F18.imprint","IMPRINT",FACE,{"disambiguationData":[TD([[makeQuery(id+"F18.imprint","IMPRINT",EDGE,{"derivedFrom":subQ0}),-1.0]])]});}
            var Q2;
            {var subQ0=sQuery(id+"F18.wireOp",EDGE,"E44.2.1");Q2=makeQuery(id+"F18.imprint","IMPRINT",FACE,{"disambiguationData":[TD([[makeQuery(id+"F18.imprint","IMPRINT",EDGE,{"derivedFrom":subQ0}),-1.0]])]});}
            var Q3;
            {var subQ0=sQuery(id+"F18.wireOp",EDGE,"E43");Q3=makeQuery(id+"F18.imprint","IMPRINT",FACE,{"disambiguationData":[TD([[makeQuery(id+"F18.imprint","IMPRINT",EDGE,{"derivedFrom":subQ0}),1.0]])]});}
            extrude(context, id + "F19", {"entities" : qUnion([Q0, Q1, Q2, Q3]), "operationType" : NewBodyOperationType.REMOVE, "oppositeDirection" : true, "depth" : 25 * mm, "offsetDistance" : 25 * mm});
        }
        {
            var Q0;
            Q0=makeQuery(id+"F19.boolean.opBoolean","COPY",EDGE,{"derivedFrom":makeQuery(id+"F19.opExtrude","SWEPT_EDGE",EDGE,{"disambiguationData":[OSD([sQuery(id+"F18.wireOp",EDGE,"E37"),sQuery(id+"F18.wireOp",EDGE,"E44.2.1")])]})});
            var Q1;
            Q1=makeQuery(id+"F19.boolean.opBoolean","COPY",EDGE,{"derivedFrom":makeQuery(id+"F19.opExtrude","SWEPT_EDGE",EDGE,{"disambiguationData":[OSD([sQuery(id+"F18.wireOp",EDGE,"E37"),sQuery(id+"F18.wireOp",EDGE,"E44.2.0")])]})});
            var Q2;
            Q2=makeQuery(id+"F19.boolean.opBoolean","COPY",EDGE,{"derivedFrom":makeQuery(id+"F19.opExtrude","SWEPT_EDGE",EDGE,{"disambiguationData":[OSD([sQuery(id+"F18.wireOp",EDGE,"E37"),sQuery(id+"F18.wireOp",EDGE,"E44.1.1")])]})});
            var Q3;
            Q3=makeQuery(id+"F19.boolean.opBoolean","COPY",EDGE,{"derivedFrom":makeQuery(id+"F19.opExtrude","SWEPT_EDGE",EDGE,{"disambiguationData":[OSD([sQuery(id+"F18.wireOp",EDGE,"E37"),sQuery(id+"F18.wireOp",EDGE,"E44.1.0")])]})});
            var Q4;
            Q4=makeQuery(id+"F19.boolean.opBoolean","COPY",EDGE,{"derivedFrom":makeQuery(id+"F19.opExtrude","SWEPT_EDGE",EDGE,{"disambiguationData":[OSD([sQuery(id+"F18.wireOp",EDGE,"E37"),sQuery(id+"F18.wireOp",EDGE,"E42")])]})});
            var Q5;
            Q5=makeQuery(id+"F19.boolean.opBoolean","COPY",EDGE,{"derivedFrom":makeQuery(id+"F19.opExtrude","SWEPT_EDGE",EDGE,{"disambiguationData":[OSD([sQuery(id+"F18.wireOp",EDGE,"E37"),sQuery(id+"F18.wireOp",EDGE,"E43")])]})});
            var Q6;
            Q6=makeQuery(id+"F19.boolean.opBoolean","COPY",EDGE,{"derivedFrom":makeQuery(id+"F19.opExtrude","SWEPT_EDGE",EDGE,{"disambiguationData":[OSD([sQuery(id+"F18.wireOp",EDGE,"E37"),sQuery(id+"F18.wireOp",EDGE,"E44.3.1")])]})});
            var Q7;
            Q7=makeQuery(id+"F19.boolean.opBoolean","COPY",EDGE,{"derivedFrom":makeQuery(id+"F19.opExtrude","SWEPT_EDGE",EDGE,{"disambiguationData":[OSD([sQuery(id+"F18.wireOp",EDGE,"E37"),sQuery(id+"F18.wireOp",EDGE,"E44.3.0")])]})});
            var Q8;
            Q8=makeQuery(id+"F19.boolean.opBoolean","COPY",EDGE,{"derivedFrom":makeQuery(id+"F19.opExtrude","SWEPT_EDGE",EDGE,{"disambiguationData":[OSD([sQuery(id+"F18.wireOp",EDGE,"E36"),sQuery(id+"F18.wireOp",EDGE,"E44.2.1")])]})});
            var Q9;
            Q9=makeQuery(id+"F19.boolean.opBoolean","COPY",EDGE,{"derivedFrom":makeQuery(id+"F19.opExtrude","SWEPT_EDGE",EDGE,{"disambiguationData":[OSD([sQuery(id+"F18.wireOp",EDGE,"E36"),sQuery(id+"F18.wireOp",EDGE,"E44.2.0")])]})});
            var Q10;
            Q10=makeQuery(id+"F19.boolean.opBoolean","COPY",EDGE,{"derivedFrom":makeQuery(id+"F19.opExtrude","SWEPT_EDGE",EDGE,{"disambiguationData":[OSD([sQuery(id+"F18.wireOp",EDGE,"E36"),sQuery(id+"F18.wireOp",EDGE,"E44.1.1")])]})});
            var Q11;
            Q11=makeQuery(id+"F19.boolean.opBoolean","COPY",EDGE,{"derivedFrom":makeQuery(id+"F19.opExtrude","SWEPT_EDGE",EDGE,{"disambiguationData":[OSD([sQuery(id+"F18.wireOp",EDGE,"E36"),sQuery(id+"F18.wireOp",EDGE,"E44.1.0")])]})});
            var Q12;
            Q12=makeQuery(id+"F19.boolean.opBoolean","COPY",EDGE,{"derivedFrom":makeQuery(id+"F19.opExtrude","SWEPT_EDGE",EDGE,{"disambiguationData":[OSD([sQuery(id+"F18.wireOp",EDGE,"E36"),sQuery(id+"F18.wireOp",EDGE,"E42")])]})});
            var Q13;
            Q13=makeQuery(id+"F19.boolean.opBoolean","COPY",EDGE,{"derivedFrom":makeQuery(id+"F19.opExtrude","SWEPT_EDGE",EDGE,{"disambiguationData":[OSD([sQuery(id+"F18.wireOp",EDGE,"E36"),sQuery(id+"F18.wireOp",EDGE,"E43")])]})});
            var Q14;
            Q14=makeQuery(id+"F19.boolean.opBoolean","COPY",EDGE,{"derivedFrom":makeQuery(id+"F19.opExtrude","SWEPT_EDGE",EDGE,{"disambiguationData":[OSD([sQuery(id+"F18.wireOp",EDGE,"E36"),sQuery(id+"F18.wireOp",EDGE,"E44.3.1")])]})});
            var Q15;
            Q15=makeQuery(id+"F19.boolean.opBoolean","COPY",EDGE,{"derivedFrom":makeQuery(id+"F19.opExtrude","SWEPT_EDGE",EDGE,{"disambiguationData":[OSD([sQuery(id+"F18.wireOp",EDGE,"E36"),sQuery(id+"F18.wireOp",EDGE,"E44.3.0")])]})});
            fillet(context, id + "F20", {"entities" : qUnion([Q0, Q1, Q2, Q3, Q4, Q5, Q6, Q7, Q8, Q9, Q10, Q11, Q12, Q13, Q14, Q15]), "radius" : 5 * mm, "tangentPropagation" : true, "allowEdgeOverflow" : false});
        }
        {
            var Q0;
            {var subQ0=sQuery(id+"F0.wireOp",EDGE,"E7.1.5");Q0=makeQuery(id+"F13.opBoolean","MERGE",FACE,{"derivedFrom":[makeQuery(id+"F8.opPattern","COPY",FACE,{"derivedFrom":makeQuery(id+"F1.opExtrude","SWEPT_FACE",FACE,{"disambiguationData":[OSD([subQ0])]}),"instanceName":"1"}),makeQuery(id+"F12.opExtrude","SWEPT_FACE",FACE,{"disambiguationData":[OSD([subQ0,sQuery(id+"F11.wireOp",EDGE,"E29.2.0")])]})]});}
            var sketch = newSketch(context, id + "F21", { "sketchPlane" : qUnion([Q0])});
            skLineSegment(sketch, "E45.bottom", {"start": v(-50.43, 4.85) * mm, "end": v(-35.43, 4.85) * mm});
            skLineSegment(sketch, "E45.top", {"start": v(-50.43, 3.85) * mm, "end": v(-35.43, 3.85) * mm});
            skLineSegment(sketch, "E45.left", {"start": v(-50.43, 4.85) * mm, "end": v(-50.43, 3.85) * mm});
            skLineSegment(sketch, "E45.right", {"start": v(-35.43, 4.85) * mm, "end": v(-35.43, 3.85) * mm});
            skPoint(sketch, "E45.middle", {"position": v(-42.93, 4.35) * mm});
            skLineSegment(sketch, "E46.0", {"start": v(-50, 9.85) * mm, "end": v(50, 9.85) * mm, "construction": true});
            skLineSegment(sketch, "E47.MirrorCS", {"start": v(-50.43, 15.85) * mm, "end": v(-35.43, 15.85) * mm});
            skLineSegment(sketch, "E48.MirrorCS", {"start": v(-35.43, 14.85) * mm, "end": v(-35.43, 15.85) * mm});
            skLineSegment(sketch, "E49.MirrorCS", {"start": v(-50.43, 14.85) * mm, "end": v(-50.43, 15.85) * mm});
            skLineSegment(sketch, "E50.MirrorCS", {"start": v(-50.43, 14.85) * mm, "end": v(-35.43, 14.85) * mm});
            skSolve(sketch);
        }
        {
            var Q0;
            Q0=makeQuery(id+"F21.imprint","IMPRINT",FACE,{"disambiguationData":[TD([[makeQuery(id+"F21.imprint","IMPRINT",EDGE,{"derivedFrom":sQuery(id+"F21.wireOp",EDGE,"E45.bottom")}),-1.0]])]});
            var Q1;
            Q1=sQuery(id+"F21.wireOp",EDGE,"E45.bottom");
            revolve(context, id + "F22", {"operationType" : NewBodyOperationType.REMOVE, "surfaceOperationType" : NewSurfaceOperationType.NEW, "entities" : qUnion([Q0]), "axis" : qUnion([Q1]), "revolveType" : RevolveType.FULL, "oppositeDirection" : true});
        }
        {
            var Q0;
            Q0=makeQuery(id+"F21.imprint","IMPRINT",FACE,{"disambiguationData":[TD([[makeQuery(id+"F21.imprint","IMPRINT",EDGE,{"derivedFrom":sQuery(id+"F21.wireOp",EDGE,"E47.MirrorCS")}),-1.0]])]});
            var Q1;
            Q1=sQuery(id+"F21.wireOp",EDGE,"E47.MirrorCS");
            revolve(context, id + "F23", {"operationType" : NewBodyOperationType.REMOVE, "surfaceOperationType" : NewSurfaceOperationType.NEW, "entities" : qUnion([Q0]), "axis" : qUnion([Q1]), "revolveType" : RevolveType.FULL, "oppositeDirection" : true});
        }
    });
